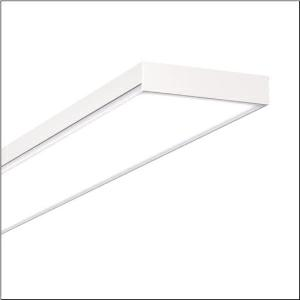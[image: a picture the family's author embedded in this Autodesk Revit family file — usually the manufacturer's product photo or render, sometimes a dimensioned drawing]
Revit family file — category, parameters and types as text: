
# Revit family: apollon_r__31_surface_51mp25wd2441w_33c1
name_source: partatom
category: Lighting Fixtures
units: mm (PartAtom-declared; Revit-internal decimal feet)

## family parameters
Cut with Voids When Loaded = No
Host = Face
Light Source = No
Part Type = Normal
Room Calculation Point = No
Round Connector Dimension = Use Diameter
Shared = No

## types (1)
- Apollon® 31 Surface (1 x LED, 3800 lm, 28 W, 4000K)
    Apparent Load = 28 VA
    CIE Flux Codes = 61 87 97 97 100
    Color Rendering = 80
    Color Temperature = 4000K
    Default Elevation = 1800 mm
    Description = Apollon® 31 Surface, office luminaire, primary optical cover: micro prismatic cover, of PMMA, light emission: direct distribution, primary light characteristic: symmetric, installation type: surface-mounted, LED, rated luminous flux: 3.800lm, luminous efficacy: 134lm/W, light colour: 840, colour temperature: 4000K, control gear: ECG DALI, with terminal, 5-pole, mains connection: 220..240V, AC, 50/60Hz, rated input power: 28W, housing, of sheet steel, coil coated, traffic white (RAL 9016), length: 1.245mm, width: 200mm, height: 44mm, protection rating (complete): IP20, insulation class (complete): insulation class II (safety insulation), certification: CE, impact resistance: IK02, permissible operating ambient temperature: -20..+40°C, standard: EN 60598-2-22, packaging unit: 1 piece
    Height = 44 mm
    Lamp = 1 x LED
    Lamp Light Flux = 3800 lm
    Lamp Power = 28 W
    Lamp count = 1
    Length = 1245 mm
    Luminous efficacy = 136 lm/W
    Manufacturer = Siteco
    ModVariant = No
    Model = 51MP25WD2441W
    Mounting Place = Ceiling
    Mounting Type = Surface mounted
    Number of Poles = 1
    OnlyDefault = Yes
    Power Factor = 1
    Product Name = Apollon® 31 Surface
    Product group = office luminaire | ceiling mounted
    ProductGroupID = 304
    Protection Class = Protection class II
    Protection Degree = IP 20
    RLX_Detail_Level = 1
    RLX_Emergency_Light_Flux = 0 lm
    RLX_Emergency_Type = 0
    RLX_Emergency_Type_DB = No
    RlxData = <blob elided: 20769 chars, md5=ed6c1862>
    Socket = socket
    Standby Power = 0 W
    System Light Flux = 3800 lm
    System Power = 28 W
    Type Comments = Product without accessories
    Type Image = l_1007095.jpg
    URL = http://relux.com
    VarID = ---
    Voltage = 0 V
    Weight = 0.00 kg
    Width = 200 mm  [stored 0.656168 ft]

note: [stored X ft] marks values corroborated as IEEE doubles in the binary element streams (Revit-internal decimal feet)

## geometry (parser evidence)
native form markers: Blend x4, Sweep x13
no freeform markers — native parametric forms only
